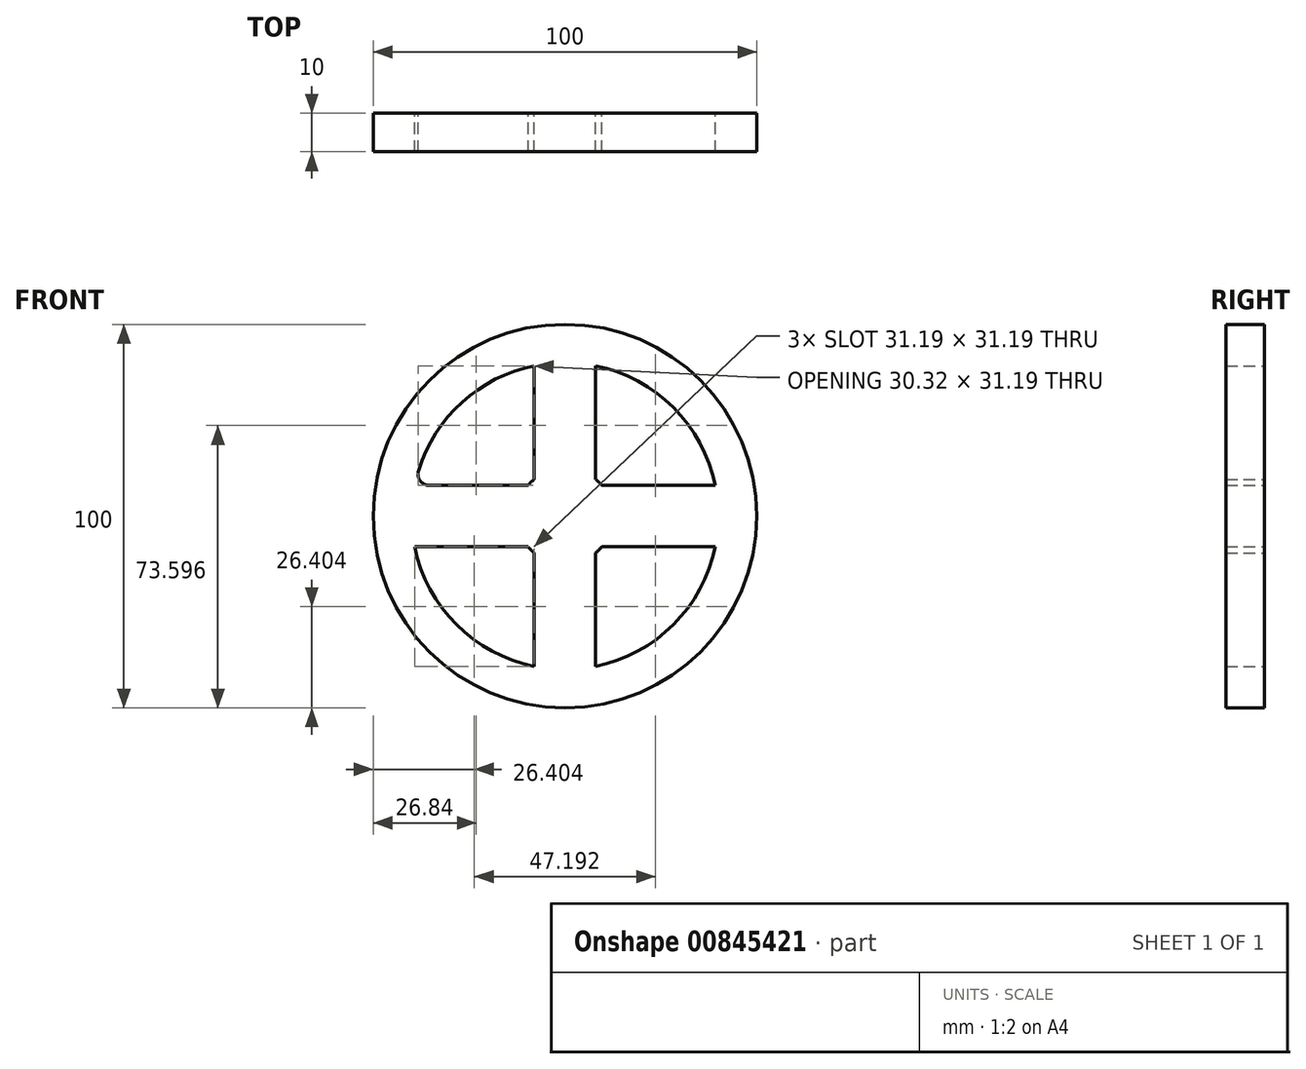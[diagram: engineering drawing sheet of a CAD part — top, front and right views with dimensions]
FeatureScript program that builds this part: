
annotation { "Feature Type Name" : "Feature", "Feature Type Description" : "" }
export const myFeature = defineFeature(function(context is Context, id is Id, definition is map)
    precondition{}
    {
        {
            var Q0;
            Q0=qCreatedBy(makeId("Front.planeOp"),FACE);
            var sketch = newSketch(context, id + "F0", { "sketchPlane" : qUnion([Q0])});
            skCircle(sketch, "E0", {"center": v(0, 0) * mm, "radius": 50 * mm});
            skCircle(sketch, "E1", {"center": v(0, 0) * mm, "radius": 40 * mm});
            skCircle(sketch, "E2", {"center": v(0, 0) * mm, "radius": 12.5 * mm});
            skCircle(sketch, "E3", {"center": v(0, 0) * mm, "radius": 5 * mm});
            skLineSegment(sketch, "E4", {"start": v(0, 0) * mm, "end": v(0, 50) * mm});
            skLineSegment(sketch, "E5", {"start": v(0, 0) * mm, "end": v(50, 0) * mm});
            skLineSegment(sketch, "E6", {"start": v(0, 0) * mm, "end": v(0, -50) * mm});
            skLineSegment(sketch, "E7", {"start": v(0, 0) * mm, "end": v(-50, 0) * mm});
            skLineSegment(sketch, "E8.0", {"start": v(8, 0) * mm, "end": v(8, 50) * mm});
            skLineSegment(sketch, "E9.0", {"start": v(0, -8) * mm, "end": v(50, -8) * mm});
            skLineSegment(sketch, "E10.0", {"start": v(0, 8) * mm, "end": v(50, 8) * mm});
            skLineSegment(sketch, "E11.0", {"start": v(-8, 0) * mm, "end": v(-8, -50) * mm});
            skLineSegment(sketch, "E12.0", {"start": v(8, 0) * mm, "end": v(8, -50) * mm});
            skLineSegment(sketch, "E13.0", {"start": v(0, 8) * mm, "end": v(-50, 8) * mm});
            skLineSegment(sketch, "E14.0", {"start": v(0, -8) * mm, "end": v(-50, -8) * mm});
            skLineSegment(sketch, "E15.0", {"start": v(-8, 0) * mm, "end": v(-8, 50) * mm});
            skSolve(sketch);
        }
        {
            var Q0;
            {var subQ0=sQuery(id+"F0.wireOp",EDGE,"E15.0");var subQ1=sQuery(id+"F0.wireOp",EDGE,"E0");var subQ2=makeQuery(id+"F0.imprint","INTERSECT",VERTEX,{"derivedFrom":[subQ1,subQ0]});Q0=makeQuery(id+"F0.imprint","IMPRINT",FACE,{"disambiguationData":[TD([[makeQuery(id+"F0.imprint","IMPRINT",EDGE,{"disambiguationData":[TD([[subQ2,-1.0]])],"derivedFrom":subQ1}),1.0]])]});}
            var Q1;
            {var subQ3=sQuery(id+"F0.wireOp",EDGE,"E3");var subQ6=sQuery(id+"F0.wireOp",EDGE,"E5");var subQ8=makeQuery(id+"F0.imprint","INTERSECT",VERTEX,{"derivedFrom":[subQ3,subQ6]});Q1=makeQuery(id+"F0.imprint","IMPRINT",FACE,{"disambiguationData":[TD([[makeQuery(id+"F0.imprint","IMPRINT",EDGE,{"disambiguationData":[TD([[subQ8,1.0]])],"derivedFrom":subQ3}),-1.0]])]});}
            var Q2;
            {var subQ0=sQuery(id+"F0.wireOp",EDGE,"E12.0");var subQ1=sQuery(id+"F0.wireOp",EDGE,"E2");var subQ2=makeQuery(id+"F0.imprint","INTERSECT",VERTEX,{"derivedFrom":[subQ1,subQ0]});Q2=makeQuery(id+"F0.imprint","IMPRINT",FACE,{"disambiguationData":[TD([[makeQuery(id+"F0.imprint","IMPRINT",EDGE,{"disambiguationData":[TD([[subQ2,-1.0]])],"derivedFrom":subQ1}),1.0]])]});}
            var Q3;
            {var subQ0=sQuery(id+"F0.wireOp",EDGE,"E5");var subQ1=sQuery(id+"F0.wireOp",EDGE,"E2");var subQ2=makeQuery(id+"F0.imprint","INTERSECT",VERTEX,{"derivedFrom":[subQ1,subQ0]});Q3=makeQuery(id+"F0.imprint","IMPRINT",FACE,{"disambiguationData":[TD([[makeQuery(id+"F0.imprint","IMPRINT",EDGE,{"disambiguationData":[TD([[subQ2,1.0]])],"derivedFrom":subQ1}),1.0]])]});}
            var Q4;
            {var subQ0=sQuery(id+"F0.wireOp",EDGE,"E11.0");var subQ1=sQuery(id+"F0.wireOp",EDGE,"E2");var subQ2=makeQuery(id+"F0.imprint","INTERSECT",VERTEX,{"derivedFrom":[subQ1,subQ0]});Q4=makeQuery(id+"F0.imprint","IMPRINT",FACE,{"disambiguationData":[TD([[makeQuery(id+"F0.imprint","IMPRINT",EDGE,{"disambiguationData":[TD([[subQ2,-1.0]])],"derivedFrom":subQ1}),1.0]])]});}
            var Q5;
            {var subQ5=sQuery(id+"F0.wireOp",EDGE,"E3");var subQ7=sQuery(id+"F0.wireOp",EDGE,"E4");var subQ9=makeQuery(id+"F0.imprint","INTERSECT",VERTEX,{"derivedFrom":[subQ5,subQ7]});Q5=makeQuery(id+"F0.imprint","IMPRINT",FACE,{"disambiguationData":[TD([[makeQuery(id+"F0.imprint","IMPRINT",EDGE,{"disambiguationData":[TD([[subQ9,1.0]])],"derivedFrom":subQ5}),-1.0]])]});}
            var Q6;
            {var subQ0=sQuery(id+"F0.wireOp",EDGE,"E10.0");var subQ1=sQuery(id+"F0.wireOp",EDGE,"E2");var subQ2=makeQuery(id+"F0.imprint","INTERSECT",VERTEX,{"derivedFrom":[subQ1,subQ0]});Q6=makeQuery(id+"F0.imprint","IMPRINT",FACE,{"disambiguationData":[TD([[makeQuery(id+"F0.imprint","IMPRINT",EDGE,{"disambiguationData":[TD([[subQ2,1.0]])],"derivedFrom":subQ1}),1.0]])]});}
            var Q7;
            {var subQ0=sQuery(id+"F0.wireOp",EDGE,"E10.0");var subQ1=sQuery(id+"F0.wireOp",EDGE,"E1");var subQ2=makeQuery(id+"F0.imprint","INTERSECT",VERTEX,{"derivedFrom":[subQ1,subQ0]});Q7=makeQuery(id+"F0.imprint","IMPRINT",FACE,{"disambiguationData":[TD([[makeQuery(id+"F0.imprint","IMPRINT",EDGE,{"disambiguationData":[TD([[subQ2,1.0]])],"derivedFrom":subQ1}),1.0]])]});}
            var Q8;
            {var subQ0=sQuery(id+"F0.wireOp",EDGE,"E6");var subQ1=sQuery(id+"F0.wireOp",EDGE,"E2");var subQ2=makeQuery(id+"F0.imprint","INTERSECT",VERTEX,{"derivedFrom":[subQ1,subQ0]});Q8=makeQuery(id+"F0.imprint","IMPRINT",FACE,{"disambiguationData":[TD([[makeQuery(id+"F0.imprint","IMPRINT",EDGE,{"disambiguationData":[TD([[subQ2,-1.0]])],"derivedFrom":subQ1}),1.0]])]});}
            var Q9;
            {var subQ0=sQuery(id+"F0.wireOp",EDGE,"E14.0");var subQ1=sQuery(id+"F0.wireOp",EDGE,"E2");var subQ2=makeQuery(id+"F0.imprint","INTERSECT",VERTEX,{"derivedFrom":[subQ1,subQ0]});Q9=makeQuery(id+"F0.imprint","IMPRINT",FACE,{"disambiguationData":[TD([[makeQuery(id+"F0.imprint","IMPRINT",EDGE,{"disambiguationData":[TD([[subQ2,-1.0]])],"derivedFrom":subQ1}),1.0]])]});}
            var Q10;
            {var subQ1=sQuery(id+"F0.wireOp",EDGE,"E7");var subQ5=sQuery(id+"F0.wireOp",EDGE,"E3");var subQ6=makeQuery(id+"F0.imprint","INTERSECT",VERTEX,{"derivedFrom":[subQ5,subQ1]});Q10=makeQuery(id+"F0.imprint","IMPRINT",FACE,{"disambiguationData":[TD([[makeQuery(id+"F0.imprint","IMPRINT",EDGE,{"disambiguationData":[TD([[subQ6,-1.0]])],"derivedFrom":subQ5}),-1.0]])]});}
            var Q11;
            {var subQ0=sQuery(id+"F0.wireOp",EDGE,"E7");var subQ1=sQuery(id+"F0.wireOp",EDGE,"E2");var subQ2=makeQuery(id+"F0.imprint","INTERSECT",VERTEX,{"derivedFrom":[subQ1,subQ0]});Q11=makeQuery(id+"F0.imprint","IMPRINT",FACE,{"disambiguationData":[TD([[makeQuery(id+"F0.imprint","IMPRINT",EDGE,{"disambiguationData":[TD([[subQ2,-1.0]])],"derivedFrom":subQ1}),1.0]])]});}
            var Q12;
            {var subQ1=sQuery(id+"F0.wireOp",EDGE,"E4");var subQ7=sQuery(id+"F0.wireOp",EDGE,"E3");var subQ9=makeQuery(id+"F0.imprint","INTERSECT",VERTEX,{"derivedFrom":[subQ7,subQ1]});Q12=makeQuery(id+"F0.imprint","IMPRINT",FACE,{"disambiguationData":[TD([[makeQuery(id+"F0.imprint","IMPRINT",EDGE,{"disambiguationData":[TD([[subQ9,-1.0]])],"derivedFrom":subQ7}),-1.0]])]});}
            var Q13;
            {var subQ0=sQuery(id+"F0.wireOp",EDGE,"E13.0");var subQ1=sQuery(id+"F0.wireOp",EDGE,"E2");var subQ2=makeQuery(id+"F0.imprint","INTERSECT",VERTEX,{"derivedFrom":[subQ1,subQ0]});Q13=makeQuery(id+"F0.imprint","IMPRINT",FACE,{"disambiguationData":[TD([[makeQuery(id+"F0.imprint","IMPRINT",EDGE,{"disambiguationData":[TD([[subQ2,-1.0]])],"derivedFrom":subQ1}),1.0]])]});}
            var Q14;
            {var subQ0=sQuery(id+"F0.wireOp",EDGE,"E15.0");var subQ1=sQuery(id+"F0.wireOp",EDGE,"E2");var subQ2=makeQuery(id+"F0.imprint","INTERSECT",VERTEX,{"derivedFrom":[subQ1,subQ0]});Q14=makeQuery(id+"F0.imprint","IMPRINT",FACE,{"disambiguationData":[TD([[makeQuery(id+"F0.imprint","IMPRINT",EDGE,{"disambiguationData":[TD([[subQ2,-1.0]])],"derivedFrom":subQ1}),1.0]])]});}
            var Q15;
            {var subQ0=sQuery(id+"F0.wireOp",EDGE,"E4");var subQ1=sQuery(id+"F0.wireOp",EDGE,"E2");var subQ2=makeQuery(id+"F0.imprint","INTERSECT",VERTEX,{"derivedFrom":[subQ1,subQ0]});Q15=makeQuery(id+"F0.imprint","IMPRINT",FACE,{"disambiguationData":[TD([[makeQuery(id+"F0.imprint","IMPRINT",EDGE,{"disambiguationData":[TD([[subQ2,-1.0]])],"derivedFrom":subQ1}),1.0]])]});}
            var Q16;
            {var subQ0=sQuery(id+"F0.wireOp",EDGE,"E8.0");var subQ1=sQuery(id+"F0.wireOp",EDGE,"E2");var subQ2=makeQuery(id+"F0.imprint","INTERSECT",VERTEX,{"derivedFrom":[subQ1,subQ0]});Q16=makeQuery(id+"F0.imprint","IMPRINT",FACE,{"disambiguationData":[TD([[makeQuery(id+"F0.imprint","IMPRINT",EDGE,{"disambiguationData":[TD([[subQ2,-1.0]])],"derivedFrom":subQ1}),1.0]])]});}
            var Q17;
            {var subQ0=sQuery(id+"F0.wireOp",EDGE,"E10.0");var subQ1=sQuery(id+"F0.wireOp",EDGE,"E2");var subQ2=makeQuery(id+"F0.imprint","INTERSECT",VERTEX,{"derivedFrom":[subQ1,subQ0]});Q17=makeQuery(id+"F0.imprint","IMPRINT",FACE,{"disambiguationData":[TD([[makeQuery(id+"F0.imprint","IMPRINT",EDGE,{"disambiguationData":[TD([[subQ2,-1.0]])],"derivedFrom":subQ1}),1.0]])]});}
            var Q18;
            {var subQ0=sQuery(id+"F0.wireOp",EDGE,"E5");var subQ1=sQuery(id+"F0.wireOp",EDGE,"E1");var subQ2=makeQuery(id+"F0.imprint","INTERSECT",VERTEX,{"derivedFrom":[subQ1,subQ0]});Q18=makeQuery(id+"F0.imprint","IMPRINT",FACE,{"disambiguationData":[TD([[makeQuery(id+"F0.imprint","IMPRINT",EDGE,{"disambiguationData":[TD([[subQ2,1.0]])],"derivedFrom":subQ1}),1.0]])]});}
            var Q19;
            {var subQ0=sQuery(id+"F0.wireOp",EDGE,"E13.0");var subQ1=sQuery(id+"F0.wireOp",EDGE,"E1");var subQ2=makeQuery(id+"F0.imprint","INTERSECT",VERTEX,{"derivedFrom":[subQ1,subQ0]});Q19=makeQuery(id+"F0.imprint","IMPRINT",FACE,{"disambiguationData":[TD([[makeQuery(id+"F0.imprint","IMPRINT",EDGE,{"disambiguationData":[TD([[subQ2,-1.0]])],"derivedFrom":subQ1}),1.0]])]});}
            var Q20;
            {var subQ0=sQuery(id+"F0.wireOp",EDGE,"E7");var subQ1=sQuery(id+"F0.wireOp",EDGE,"E1");var subQ2=makeQuery(id+"F0.imprint","INTERSECT",VERTEX,{"derivedFrom":[subQ1,subQ0]});Q20=makeQuery(id+"F0.imprint","IMPRINT",FACE,{"disambiguationData":[TD([[makeQuery(id+"F0.imprint","IMPRINT",EDGE,{"disambiguationData":[TD([[subQ2,-1.0]])],"derivedFrom":subQ1}),1.0]])]});}
            var Q21;
            {var subQ0=sQuery(id+"F0.wireOp",EDGE,"E4");var subQ1=sQuery(id+"F0.wireOp",EDGE,"E1");var subQ2=makeQuery(id+"F0.imprint","INTERSECT",VERTEX,{"derivedFrom":[subQ1,subQ0]});Q21=makeQuery(id+"F0.imprint","IMPRINT",FACE,{"disambiguationData":[TD([[makeQuery(id+"F0.imprint","IMPRINT",EDGE,{"disambiguationData":[TD([[subQ2,-1.0]])],"derivedFrom":subQ1}),1.0]])]});}
            var Q22;
            {var subQ0=sQuery(id+"F0.wireOp",EDGE,"E8.0");var subQ1=sQuery(id+"F0.wireOp",EDGE,"E1");var subQ2=makeQuery(id+"F0.imprint","INTERSECT",VERTEX,{"derivedFrom":[subQ1,subQ0]});Q22=makeQuery(id+"F0.imprint","IMPRINT",FACE,{"disambiguationData":[TD([[makeQuery(id+"F0.imprint","IMPRINT",EDGE,{"disambiguationData":[TD([[subQ2,-1.0]])],"derivedFrom":subQ1}),1.0]])]});}
            var Q23;
            {var subQ0=sQuery(id+"F0.wireOp",EDGE,"E11.0");var subQ1=sQuery(id+"F0.wireOp",EDGE,"E1");var subQ2=makeQuery(id+"F0.imprint","INTERSECT",VERTEX,{"derivedFrom":[subQ1,subQ0]});Q23=makeQuery(id+"F0.imprint","IMPRINT",FACE,{"disambiguationData":[TD([[makeQuery(id+"F0.imprint","IMPRINT",EDGE,{"disambiguationData":[TD([[subQ2,-1.0]])],"derivedFrom":subQ1}),1.0]])]});}
            var Q24;
            {var subQ0=sQuery(id+"F0.wireOp",EDGE,"E6");var subQ1=sQuery(id+"F0.wireOp",EDGE,"E1");var subQ2=makeQuery(id+"F0.imprint","INTERSECT",VERTEX,{"derivedFrom":[subQ1,subQ0]});Q24=makeQuery(id+"F0.imprint","IMPRINT",FACE,{"disambiguationData":[TD([[makeQuery(id+"F0.imprint","IMPRINT",EDGE,{"disambiguationData":[TD([[subQ2,-1.0]])],"derivedFrom":subQ1}),1.0]])]});}
            var Q25;
            {var subQ0=sQuery(id+"F0.wireOp",EDGE,"E14.0");var subQ1=sQuery(id+"F0.wireOp",EDGE,"E0");var subQ2=makeQuery(id+"F0.imprint","INTERSECT",VERTEX,{"derivedFrom":[subQ1,subQ0]});Q25=makeQuery(id+"F0.imprint","IMPRINT",FACE,{"disambiguationData":[TD([[makeQuery(id+"F0.imprint","IMPRINT",EDGE,{"disambiguationData":[TD([[subQ2,-1.0]])],"derivedFrom":subQ1}),1.0]])]});}
            var Q26;
            {var subQ0=sQuery(id+"F0.wireOp",EDGE,"E7");var subQ1=sQuery(id+"F0.wireOp",EDGE,"E0");var subQ2=makeQuery(id+"F0.imprint","INTERSECT",VERTEX,{"derivedFrom":[subQ1,subQ0]});Q26=makeQuery(id+"F0.imprint","IMPRINT",FACE,{"disambiguationData":[TD([[makeQuery(id+"F0.imprint","IMPRINT",EDGE,{"disambiguationData":[TD([[subQ2,1.0]])],"derivedFrom":subQ1}),1.0]])]});}
            var Q27;
            {var subQ0=sQuery(id+"F0.wireOp",EDGE,"E7");var subQ1=sQuery(id+"F0.wireOp",EDGE,"E0");var subQ2=makeQuery(id+"F0.imprint","INTERSECT",VERTEX,{"derivedFrom":[subQ1,subQ0]});Q27=makeQuery(id+"F0.imprint","IMPRINT",FACE,{"disambiguationData":[TD([[makeQuery(id+"F0.imprint","IMPRINT",EDGE,{"disambiguationData":[TD([[subQ2,-1.0]])],"derivedFrom":subQ1}),1.0]])]});}
            var Q28;
            {var subQ0=sQuery(id+"F0.wireOp",EDGE,"E4");var subQ1=sQuery(id+"F0.wireOp",EDGE,"E0");var subQ2=makeQuery(id+"F0.imprint","INTERSECT",VERTEX,{"derivedFrom":[subQ1,subQ0]});Q28=makeQuery(id+"F0.imprint","IMPRINT",FACE,{"disambiguationData":[TD([[makeQuery(id+"F0.imprint","IMPRINT",EDGE,{"disambiguationData":[TD([[subQ2,-1.0]])],"derivedFrom":subQ1}),1.0]])]});}
            var Q29;
            {var subQ0=sQuery(id+"F0.wireOp",EDGE,"E4");var subQ1=sQuery(id+"F0.wireOp",EDGE,"E0");var subQ2=makeQuery(id+"F0.imprint","INTERSECT",VERTEX,{"derivedFrom":[subQ1,subQ0]});Q29=makeQuery(id+"F0.imprint","IMPRINT",FACE,{"disambiguationData":[TD([[makeQuery(id+"F0.imprint","IMPRINT",EDGE,{"disambiguationData":[TD([[subQ2,1.0]])],"derivedFrom":subQ1}),1.0]])]});}
            var Q30;
            {var subQ0=sQuery(id+"F0.wireOp",EDGE,"E10.0");var subQ1=sQuery(id+"F0.wireOp",EDGE,"E0");var subQ2=makeQuery(id+"F0.imprint","INTERSECT",VERTEX,{"derivedFrom":[subQ1,subQ0]});Q30=makeQuery(id+"F0.imprint","IMPRINT",FACE,{"disambiguationData":[TD([[makeQuery(id+"F0.imprint","IMPRINT",EDGE,{"disambiguationData":[TD([[subQ2,-1.0]])],"derivedFrom":subQ1}),1.0]])]});}
            var Q31;
            {var subQ0=sQuery(id+"F0.wireOp",EDGE,"E5");var subQ1=sQuery(id+"F0.wireOp",EDGE,"E0");var subQ2=makeQuery(id+"F0.imprint","INTERSECT",VERTEX,{"derivedFrom":[subQ1,subQ0]});Q31=makeQuery(id+"F0.imprint","IMPRINT",FACE,{"disambiguationData":[TD([[makeQuery(id+"F0.imprint","IMPRINT",EDGE,{"disambiguationData":[TD([[subQ2,-1.0]])],"derivedFrom":subQ1}),1.0]])]});}
            var Q32;
            {var subQ0=sQuery(id+"F0.wireOp",EDGE,"E5");var subQ1=sQuery(id+"F0.wireOp",EDGE,"E0");var subQ2=makeQuery(id+"F0.imprint","INTERSECT",VERTEX,{"derivedFrom":[subQ1,subQ0]});Q32=makeQuery(id+"F0.imprint","IMPRINT",FACE,{"disambiguationData":[TD([[makeQuery(id+"F0.imprint","IMPRINT",EDGE,{"disambiguationData":[TD([[subQ2,1.0]])],"derivedFrom":subQ1}),1.0]])]});}
            var Q33;
            {var subQ0=sQuery(id+"F0.wireOp",EDGE,"E12.0");var subQ1=sQuery(id+"F0.wireOp",EDGE,"E0");var subQ2=makeQuery(id+"F0.imprint","INTERSECT",VERTEX,{"derivedFrom":[subQ1,subQ0]});Q33=makeQuery(id+"F0.imprint","IMPRINT",FACE,{"disambiguationData":[TD([[makeQuery(id+"F0.imprint","IMPRINT",EDGE,{"disambiguationData":[TD([[subQ2,-1.0]])],"derivedFrom":subQ1}),1.0]])]});}
            var Q34;
            {var subQ0=sQuery(id+"F0.wireOp",EDGE,"E6");var subQ1=sQuery(id+"F0.wireOp",EDGE,"E0");var subQ2=makeQuery(id+"F0.imprint","INTERSECT",VERTEX,{"derivedFrom":[subQ1,subQ0]});Q34=makeQuery(id+"F0.imprint","IMPRINT",FACE,{"disambiguationData":[TD([[makeQuery(id+"F0.imprint","IMPRINT",EDGE,{"disambiguationData":[TD([[subQ2,1.0]])],"derivedFrom":subQ1}),1.0]])]});}
            var Q35;
            {var subQ0=sQuery(id+"F0.wireOp",EDGE,"E6");var subQ1=sQuery(id+"F0.wireOp",EDGE,"E0");var subQ2=makeQuery(id+"F0.imprint","INTERSECT",VERTEX,{"derivedFrom":[subQ1,subQ0]});Q35=makeQuery(id+"F0.imprint","IMPRINT",FACE,{"disambiguationData":[TD([[makeQuery(id+"F0.imprint","IMPRINT",EDGE,{"disambiguationData":[TD([[subQ2,-1.0]])],"derivedFrom":subQ1}),1.0]])]});}
            extrude(context, id + "F1", {"entities" : qUnion([Q0, Q1, Q2, Q3, Q4, Q5, Q6, Q7, Q8, Q9, Q10, Q11, Q12, Q13, Q14, Q15, Q16, Q17, Q18, Q19, Q20, Q21, Q22, Q23, Q24, Q25, Q26, Q27, Q28, Q29, Q30, Q31, Q32, Q33, Q34, Q35]), "depth" : 10 * mm, "offsetDistance" : 25 * mm});
        }
        {
            var Q0;
            Q0=makeQuery(id+"F1.opExtrude","CAP_FACE",FACE,{"disambiguationData":[OSD([sQuery(id+"F0.wireOp",EDGE,"E0"),sQuery(id+"F0.wireOp",EDGE,"E1"),sQuery(id+"F0.wireOp",EDGE,"E2"),sQuery(id+"F0.wireOp",EDGE,"E3"),sQuery(id+"F0.wireOp",EDGE,"E8.0"),sQuery(id+"F0.wireOp",EDGE,"E9.0"),sQuery(id+"F0.wireOp",EDGE,"E10.0"),sQuery(id+"F0.wireOp",EDGE,"E11.0"),sQuery(id+"F0.wireOp",EDGE,"E12.0"),sQuery(id+"F0.wireOp",EDGE,"E13.0"),sQuery(id+"F0.wireOp",EDGE,"E14.0"),sQuery(id+"F0.wireOp",EDGE,"E15.0")])],"isStart":false});
            var sketch = newSketch(context, id + "F2", { "sketchPlane" : qUnion([Q0])});
            skLineSegment(sketch, "E16", {"start": v(4.61, 1.93) * mm, "end": v(7.6, 1.93) * mm});
            skLineSegment(sketch, "E17", {"start": v(7.6, 1.93) * mm, "end": v(7.6, 1.93) * mm});
            skLineSegment(sketch, "E18", {"start": v(7.6, 1.93) * mm, "end": v(7.6, 0) * mm});
            skLineSegment(sketch, "E19", {"start": v(7.6, 0) * mm, "end": v(7.6, -1.93) * mm});
            skLineSegment(sketch, "E20", {"start": v(7.6, -1.93) * mm, "end": v(4.61, -1.93) * mm});
            skSolve(sketch);
        }
        {
            var Q0;
            {var subQ1=sQuery(id+"F2.wireOp",EDGE,"E16");Q0=makeQuery(id+"F2.imprint","IMPRINT",FACE,{"disambiguationData":[TD([[makeQuery(id+"F2.imprint","IMPRINT",EDGE,{"derivedFrom":subQ1}),-1.0]])]});}
            var Q1;
            {var subQ0=makeQuery(id+"F1.opExtrude","CAP_EDGE",EDGE,{"disambiguationData":[OSD([sQuery(id+"F0.wireOp",EDGE,"E3")])],"isStart":false});var subQ1=makeQuery(id+"F2.imprint","INTERSECT",VERTEX,{"derivedFrom":[subQ0,sQuery(id+"F2.wireOp",EDGE,"E16")]});Q1=makeQuery(id+"F2.imprint","IMPRINT",FACE,{"disambiguationData":[TD([[makeQuery(id+"F2.imprint","IMPRINT",EDGE,{"disambiguationData":[TD([[subQ1,1.0]])],"derivedFrom":subQ0}),1.0]])]});}
            extrude(context, id + "F3", {"entities" : qUnion([Q0, Q1]), "operationType" : NewBodyOperationType.ADD, "oppositeDirection" : true, "depth" : 10 * mm, "offsetDistance" : 25 * mm});
        }
        {
            var Q0;
            {var subQ0=sQuery(id+"F0.wireOp",EDGE,"E3");Q0=makeQuery(id+"F3.boolean.opBoolean","MERGE",FACE,{"derivedFrom":[makeQuery(id+"F1.opExtrude","CAP_FACE",FACE,{"disambiguationData":[OSD([sQuery(id+"F0.wireOp",EDGE,"E0"),sQuery(id+"F0.wireOp",EDGE,"E1"),sQuery(id+"F0.wireOp",EDGE,"E2"),subQ0,sQuery(id+"F0.wireOp",EDGE,"E8.0"),sQuery(id+"F0.wireOp",EDGE,"E9.0"),sQuery(id+"F0.wireOp",EDGE,"E10.0"),sQuery(id+"F0.wireOp",EDGE,"E11.0"),sQuery(id+"F0.wireOp",EDGE,"E12.0"),sQuery(id+"F0.wireOp",EDGE,"E13.0"),sQuery(id+"F0.wireOp",EDGE,"E14.0"),sQuery(id+"F0.wireOp",EDGE,"E15.0")])],"isStart":false}),makeQuery(id+"F3.opExtrude","CAP_FACE",FACE,{"disambiguationData":[OSD([subQ0,sQuery(id+"F2.wireOp",EDGE,"E16"),sQuery(id+"F2.wireOp",EDGE,"E18"),sQuery(id+"F2.wireOp",EDGE,"E19"),sQuery(id+"F2.wireOp",EDGE,"E20")])],"isStart":true})]});}
            var sketch = newSketch(context, id + "F4", { "sketchPlane" : qUnion([Q0])});
            skCircle(sketch, "E21", {"center": v(0, 0) * mm, "radius": 5 * mm});
            skSolve(sketch);
        }
        {
            var Q0;
            Q0=makeQuery(id+"F4.imprint","IMPRINT",FACE,{"disambiguationData":[TD([[makeQuery(id+"F4.imprint","IMPRINT",EDGE,{"derivedFrom":sQuery(id+"F4.wireOp",EDGE,"E21")}),1.0]])]});
            extrude(context, id + "F5", {"entities" : qUnion([Q0]), "operationType" : NewBodyOperationType.ADD, "oppositeDirection" : true, "depth" : 10 * mm, "offsetDistance" : 25 * mm});
        }
        {
            var Q0;
            Q0=makeQuery(id+"F1.opExtrude","SWEPT_EDGE",EDGE,{"disambiguationData":[OSD([sQuery(id+"F0.wireOp",EDGE,"E1"),sQuery(id+"F0.wireOp",EDGE,"E13.0")])]});
            fillet(context, id + "F6", {"entities" : qUnion([Q0]), "radius" : 3 * mm, "tangentPropagation" : true, "allowEdgeOverflow" : false});
        }
    });
